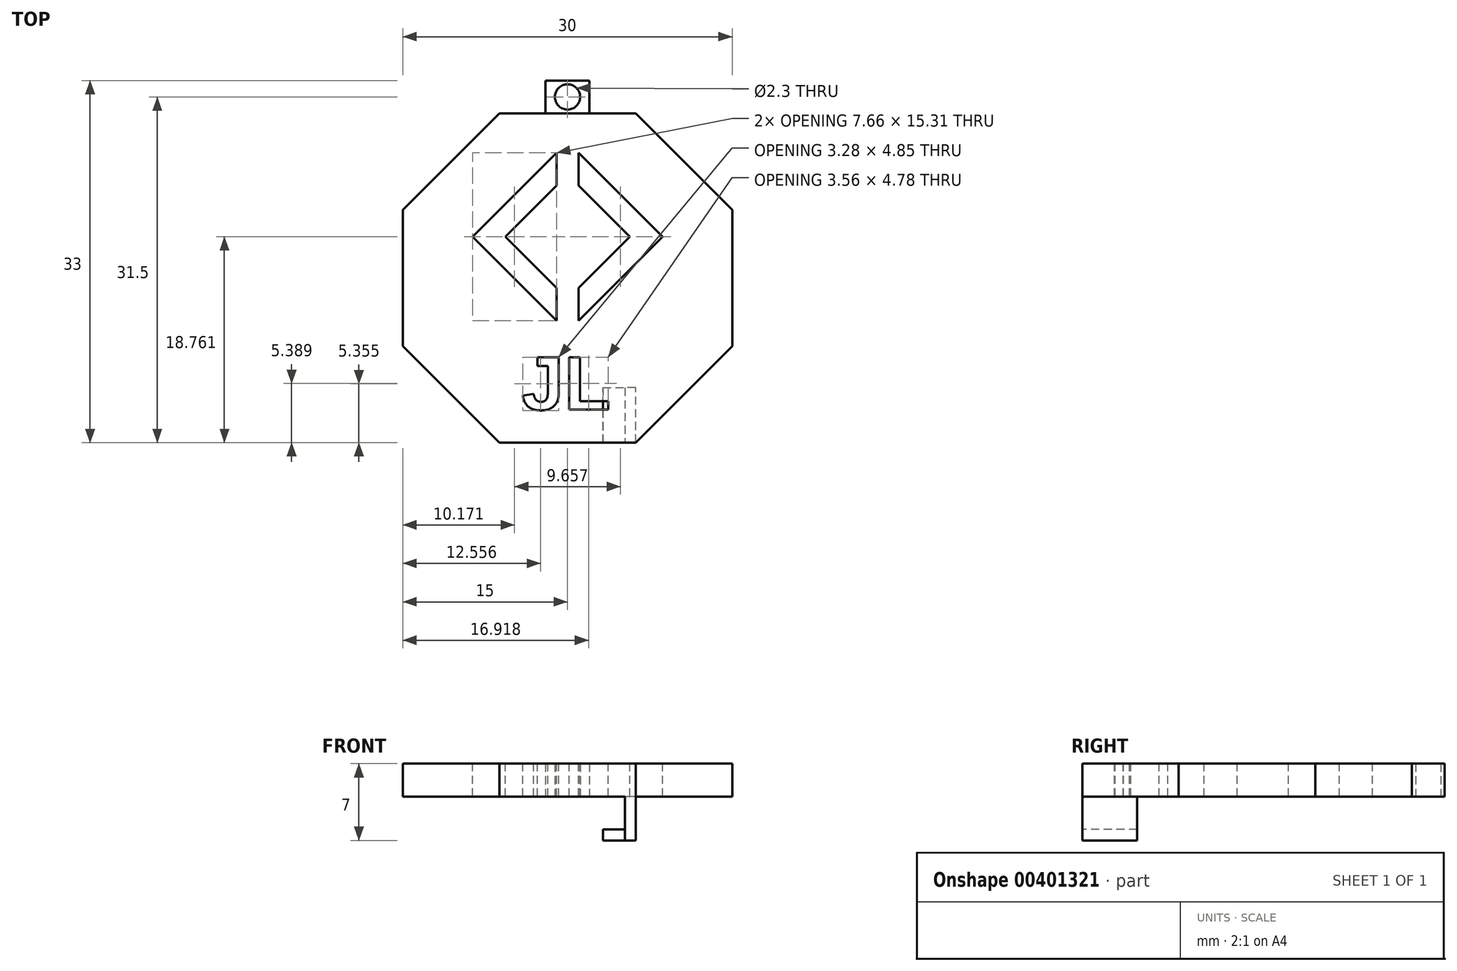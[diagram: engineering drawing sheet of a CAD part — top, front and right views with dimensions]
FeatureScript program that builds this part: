
annotation { "Feature Type Name" : "Feature", "Feature Type Description" : "" }
export const myFeature = defineFeature(function(context is Context, id is Id, definition is map)
    precondition{}
    {
        {
            var Q0;
            Q0=qCreatedBy(makeId("Top.planeOp"),FACE);
            var sketch = newSketch(context, id + "F0", { "sketchPlane" : qUnion([Q0])});
            skCircle(sketch, "E0.cCircle", {"center": v(0, 0) * mm, "radius": 15 * mm, "construction": true});
            skLineSegment(sketch, "E0.0", {"start": v(15, 6.21) * mm, "end": v(15, -6.21) * mm});
            skLineSegment(sketch, "E0.1", {"start": v(15, -6.21) * mm, "end": v(6.21, -15) * mm});
            skLineSegment(sketch, "E0.2", {"start": v(6.21, -15) * mm, "end": v(-6.21, -15) * mm});
            skLineSegment(sketch, "E0.3", {"start": v(-6.21, -15) * mm, "end": v(-15, -6.21) * mm});
            skLineSegment(sketch, "E0.4", {"start": v(-15, -6.21) * mm, "end": v(-15, 6.21) * mm});
            skLineSegment(sketch, "E0.5", {"start": v(-15, 6.21) * mm, "end": v(-6.21, 15) * mm});
            skLineSegment(sketch, "E0.6", {"start": v(-6.21, 15) * mm, "end": v(6.21, 15) * mm});
            skLineSegment(sketch, "E0.7", {"start": v(6.21, 15) * mm, "end": v(15, 6.21) * mm});
            skPoint(sketch, "E0.0.midPoint", {"position": v(15, 0) * mm});
            skLineSegment(sketch, "E1", {"start": v(0, 0) * mm, "end": v(-15, 0) * mm, "construction": true});
            skSolve(sketch);
        }
        {
            var Q0;
            Q0=qSketchRegion(id+"F0",true);
            extrude(context, id + "F1", {"entities" : qUnion([Q0]), "depth" : 3 * mm});
        }
        {
            var Q0;
            Q0=makeQuery(id+"F1.opExtrude","CAP_FACE",FACE,{"disambiguationData":[OSD([sQuery(id+"F0.wireOp",EDGE,"E0.0"),sQuery(id+"F0.wireOp",EDGE,"E0.1"),sQuery(id+"F0.wireOp",EDGE,"E0.2"),sQuery(id+"F0.wireOp",EDGE,"E0.3"),sQuery(id+"F0.wireOp",EDGE,"E0.4"),sQuery(id+"F0.wireOp",EDGE,"E0.5"),sQuery(id+"F0.wireOp",EDGE,"E0.6"),sQuery(id+"F0.wireOp",EDGE,"E0.7")])],"isStart":false});
            var sketch = newSketch(context, id + "F2", { "sketchPlane" : qUnion([Q0])});
            skText(sketch, "E2", { "text": "JL", "fontName": "Arimo-Bold.ttf"});
            skArc(sketch, "E3.cCircle", {"start": v(2.83, 0.93) * mm, "mid": v(0, 7.76) * mm, "end": v(-2.83, 0.93) * mm, "construction": true});
            skLineSegment(sketch, "E3.0", {"start": v(5.66, 3.76) * mm, "end": v(1, -0.9) * mm});
            skLineSegment(sketch, "E3.2", {"start": v(-5.66, 3.76) * mm, "end": v(-1, 8.42) * mm});
            skLineSegment(sketch, "E3.3", {"start": v(1, 8.42) * mm, "end": v(5.66, 3.76) * mm});
            skPoint(sketch, "E3.0.midPoint", {"position": v(2.83, 0.93) * mm});
            skLineSegment(sketch, "E4", {"start": v(-5.66, 3.76) * mm, "end": v(0, 3.76) * mm, "construction": true});
            skLineSegment(sketch, "E5.1", {"start": v(8.66, 3.76) * mm, "end": v(1, -3.9) * mm});
            skLineSegment(sketch, "E5.3", {"start": v(-8.66, 3.76) * mm, "end": v(-1, 11.42) * mm});
            skPoint(sketch, "E5.0.midPoint", {"position": v(4.33, 8.1) * mm});
            skLineSegment(sketch, "E6", {"start": v(-8.66, 3.76) * mm, "end": v(-5.66, 3.76) * mm, "construction": true});
            skPoint(sketch, "E7.orphan", {"position": v(0, -1.9) * mm});
            skPoint(sketch, "E8.orphan", {"position": v(0, -4.9) * mm});
            skPoint(sketch, "E9.orphan", {"position": v(0.45, -660.17) * mm});
            skPoint(sketch, "E10.orphan", {"position": v(-0.45, -23.95) * mm});
            skLineSegment(sketch, "E11.trimOffspring", {"start": v(0, 3.76) * mm, "end": v(8.66, 3.76) * mm, "construction": true});
            skPoint(sketch, "E12.orphan", {"position": v(0, 9.42) * mm});
            skPoint(sketch, "E13.orphan", {"position": v(0, 12.42) * mm});
            skPoint(sketch, "E14.bottom.end.orphan", {"position": v(0.45, 31.48) * mm});
            skPoint(sketch, "E14.bottom.start.orphan", {"position": v(-0.45, 667.69) * mm});
            skPoint(sketch, "E15.firstSnap0", {"position": v(-10.6, -10.6) * mm});
            skPoint(sketch, "E15.secondSnap0", {"position": v(10.6, 10.6) * mm});
            skPoint(sketch, "E16.startSnap0", {"position": v(0.45, 11.37) * mm});
            skLineSegment(sketch, "E17", {"start": v(1, 11.42) * mm, "end": v(1, 8.42) * mm});
            skLineSegment(sketch, "E18", {"start": v(-1, 11.42) * mm, "end": v(-1, 8.42) * mm});
            skPoint(sketch, "E19.orphan", {"position": v(0.45, 12.87) * mm});
            skLineSegment(sketch, "E20.trimOffspring", {"start": v(1, 11.42) * mm, "end": v(8.66, 3.76) * mm});
            skPoint(sketch, "E21.trimOffspring.end.orphan", {"position": v(0.45, 9.87) * mm});
            skLineSegment(sketch, "E22.trimOffspring", {"start": v(-1, -0.9) * mm, "end": v(-5.66, 3.76) * mm});
            skLineSegment(sketch, "E23.trimOffspring", {"start": v(-1, -0.9) * mm, "end": v(-1, -3.9) * mm});
            skLineSegment(sketch, "E24.trimOffspring", {"start": v(1, -0.9) * mm, "end": v(1, -3.9) * mm});
            skLineSegment(sketch, "E25.trimOffspring", {"start": v(-1, -3.9) * mm, "end": v(-8.66, 3.76) * mm});
            const initialGuessF2  = {"E2": [-0.00419, -0.012, 1, 0, 0.005]};
            skSetInitialGuess(sketch, initialGuessF2);
            skSolve(sketch);
        }
        {
            var Q0;
            Q0=qSketchRegion(id+"F2",true);
            extrude(context, id + "F3", {"entities" : qUnion([Q0]), "operationType" : NewBodyOperationType.REMOVE, "endBound" : BoundingType.THROUGH_ALL, "oppositeDirection" : true, "depth" : 3 * mm});
        }
        {
            var Q0;
            Q0=makeQuery(id+"F1.opExtrude","CAP_FACE",FACE,{"disambiguationData":[OSD([sQuery(id+"F0.wireOp",EDGE,"E0.0"),sQuery(id+"F0.wireOp",EDGE,"E0.1"),sQuery(id+"F0.wireOp",EDGE,"E0.2"),sQuery(id+"F0.wireOp",EDGE,"E0.3"),sQuery(id+"F0.wireOp",EDGE,"E0.4"),sQuery(id+"F0.wireOp",EDGE,"E0.5"),sQuery(id+"F0.wireOp",EDGE,"E0.6"),sQuery(id+"F0.wireOp",EDGE,"E0.7")])],"isStart":true});
            var sketch = newSketch(context, id + "F4", { "sketchPlane" : qUnion([Q0])});
            skLineSegment(sketch, "E26.bottom", {"start": v(6.21, 15) * mm, "end": v(5.21, 15) * mm});
            skLineSegment(sketch, "E26.top", {"start": v(6.21, 10) * mm, "end": v(5.21, 10) * mm});
            skLineSegment(sketch, "E26.left", {"start": v(6.21, 15) * mm, "end": v(6.21, 10) * mm});
            skLineSegment(sketch, "E26.right", {"start": v(5.21, 15) * mm, "end": v(5.21, 10) * mm});
            skSolve(sketch);
        }
        {
            var Q0;
            Q0=qSketchRegion(id+"F4",true);
            extrude(context, id + "F5", {"entities" : qUnion([Q0]), "operationType" : NewBodyOperationType.ADD, "depth" : 4 * mm});
        }
        {
            var Q0;
            Q0=makeQuery(id+"F5.opExtrude","SWEPT_FACE",FACE,{"disambiguationData":[OSD([sQuery(id+"F4.wireOp",EDGE,"E26.right")])]});
            var sketch = newSketch(context, id + "F6", { "sketchPlane" : qUnion([Q0])});
            skLineSegment(sketch, "E27.bottom", {"start": v(10, -4) * mm, "end": v(15, -4) * mm});
            skLineSegment(sketch, "E27.top", {"start": v(10, -3) * mm, "end": v(15, -3) * mm});
            skLineSegment(sketch, "E27.left", {"start": v(10, -4) * mm, "end": v(10, -3) * mm});
            skLineSegment(sketch, "E27.right", {"start": v(15, -4) * mm, "end": v(15, -3) * mm});
            skSolve(sketch);
        }
        {
            var Q0;
            Q0=makeQuery(id+"F6.imprint","IMPRINT",FACE,{"disambiguationData":[TD([[makeQuery(id+"F6.imprint","IMPRINT",EDGE,{"derivedFrom":sQuery(id+"F6.wireOp",EDGE,"E27.bottom")}),-1.0]])]});
            var Q1;
            Q1=sQuery(id+"F6.wireOp",EDGE,"E27.top");
            var Q2;
            Q2=sQuery(id+"F6.wireOp",EDGE,"E27.bottom");
            var Q3;
            Q3=sQuery(id+"F6.wireOp",EDGE,"E27.right");
            var Q4;
            Q4=sQuery(id+"F6.wireOp",EDGE,"E27.left");
            extrude(context, id + "F7", {"entities" : qUnion([Q0]), "surfaceEntities" : qUnion([Q1, Q2, Q3, Q4]), "depth" : 2 * mm});
        }
        {
            var Q0;
            Q0=makeQuery(id+"F1.opExtrude","SWEPT_FACE",FACE,{"disambiguationData":[OSD([sQuery(id+"F0.wireOp",EDGE,"E0.6")])]});
            var sketch = newSketch(context, id + "F8", { "sketchPlane" : qUnion([Q0])});
            skLineSegment(sketch, "E28.bottom", {"start": v(2, 3) * mm, "end": v(-2, 3) * mm});
            skLineSegment(sketch, "E28.top", {"start": v(2, 0) * mm, "end": v(-2, 0) * mm});
            skLineSegment(sketch, "E28.left", {"start": v(2, 3) * mm, "end": v(2, 0) * mm});
            skLineSegment(sketch, "E28.right", {"start": v(-2, 3) * mm, "end": v(-2, 0) * mm});
            skPoint(sketch, "E28.middle", {"position": v(0, 1.5) * mm});
            skPoint(sketch, "E28.middle.positionSnap0", {"position": v(0, 3) * mm});
            skPoint(sketch, "E28.centerSnap0", {"position": v(0, 3) * mm});
            skSolve(sketch);
        }
        {
            var Q0;
            Q0=qSketchRegion(id+"F8",true);
            extrude(context, id + "F9", {"entities" : qUnion([Q0]), "depth" : 3 * mm});
        }
        {
            var Q0;
            Q0=makeQuery(id+"F9.opExtrude","SWEPT_FACE",FACE,{"disambiguationData":[OSD([sQuery(id+"F8.wireOp",EDGE,"E28.top")])]});
            var sketch = newSketch(context, id + "F10", { "sketchPlane" : qUnion([Q0])});
            skCircle(sketch, "E29", {"center": v(0, -16.5) * mm, "radius": 1.15 * mm});
            skLineSegment(sketch, "E30", {"start": v(0, -16.5) * mm, "end": v(0, -15) * mm, "construction": true});
            skLineSegment(sketch, "E31", {"start": v(0, -16.5) * mm, "end": v(0, -18) * mm, "construction": true});
            skSolve(sketch);
        }
        {
            var Q0;
            Q0=qSketchRegion(id+"F10",true);
            extrude(context, id + "F11", {"entities" : qUnion([Q0]), "operationType" : NewBodyOperationType.REMOVE, "endBound" : BoundingType.THROUGH_ALL, "oppositeDirection" : true, "depth" : 25 * mm});
        }
    });
